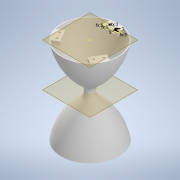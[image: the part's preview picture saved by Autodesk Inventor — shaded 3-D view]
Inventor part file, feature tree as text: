
AUTODESK INVENTOR PART (.ipt)
format: ipt  version: 2020.2 (Build 242310000, 310)  size: 483,840 bytes
history: native  units: in
note: dims shown in document units (in); Inventor stores cm internally (conversion verified against a paired STEP export)
features: sketch x4, extrude x3, fillet x2, plane x2, revolve x1, shell x1, pattern_circular x1, mirror x1
ambient origin geometry x8: Origin, YZ Plane, XZ Plane, XY Plane, X Axis, Y Axis, Z Axis, Center Point
bodies: Solid1 (feature_tree)
feature tree (15):
  revolve  "Revolution1"  [1 undecoded]
  fillet  "Fillet1"  Radius=0.3937in
  shell  "Shell2"  Thickness=3.4038in
  extrude  "Extrusion1"  Depth=4.7244in
  plane  "Work Plane2"
  extrude  "Extrusion3"  Depth=0.3937in
  extrude  "Extrusion4"  Depth=0.0394in
  fillet  "Fillet2"  Radius=0.1969in
  pattern_circular  "Circular Pattern2"  Angle=90.0deg  [1 undecoded]
  plane  "Work Plane3"
  mirror  "Mirror1"
  sketch  "Sketch3"  dims[d39=2.7559in d40=1.5748in d41=4.7244in d42=0.3937in d43=2.1654in d49=3.4038in]
  sketch  "Sketch4"  dims[d50=3.1496in d51=4.7244in]
  sketch  "Sketch6"  dims[d52=2.1654in d54=0.3937in]
  sketch  "Sketch7"  dims[d55=0.1969in d58=0.1969in d59=0.1969in d60=90.0deg d61=0.4537in d63=0.0472in d65=0.3937in d66=0.7874in d67=0.3937in d68=0.1969in d69=0.0in d83=0.0in d84=0.1181in d85=0.1181in d86=0.1969in d87=0.1969in d88=0.1969in d89=0.1969in d90=0.2362in d91=0.0in d92=0.2165in d93=0.0709in d94=0.1181in d95=0.0394in d96=0.0492in d97=0.0157in d99=0.063in d100=0.1378in d101=0.2165in d102=0.0709in d103=0.1181in d104=0.0394in d105=0.0492in d106=0.0157in d107=0.063in d108=0.1378in d109=0.3051in d110=0.0in d111=0.0394in d112=1.1811in d113=360.0deg d115=2.3622in]
note: 2 required parameter values undecoded (feature->parameter linkage not recoverable at this tier; creation-order binding heuristic only, values carry confidence <= 0.55)